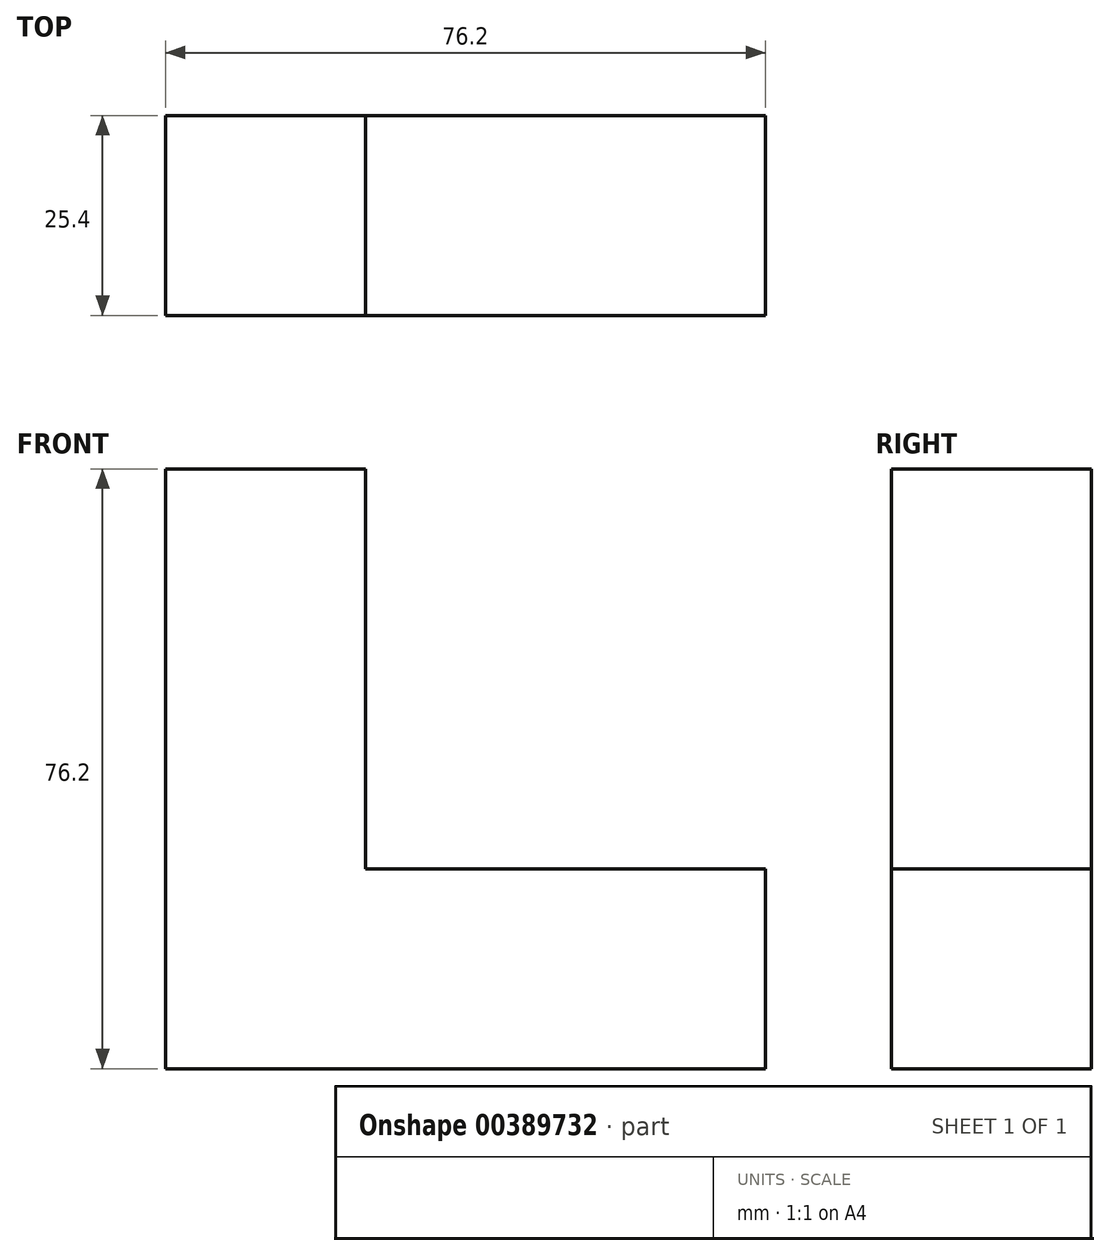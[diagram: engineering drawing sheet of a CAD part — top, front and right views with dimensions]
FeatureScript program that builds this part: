
annotation { "Feature Type Name" : "Feature", "Feature Type Description" : "" }
export const myFeature = defineFeature(function(context is Context, id is Id, definition is map)
    precondition{}
    {
        {
            var Q0;
            Q0=qCreatedBy(makeId("Front.planeOp"),FACE);
            var sketch = newSketch(context, id + "F0", { "sketchPlane" : qUnion([Q0])});
            skLineSegment(sketch, "E0.bottom", {"start": v(0, 0) * mm, "end": v(-25.4, 0) * mm});
            skLineSegment(sketch, "E0.top", {"start": v(0, 25.4) * mm, "end": v(-25.4, 25.4) * mm});
            skLineSegment(sketch, "E0.left", {"start": v(0, 0) * mm, "end": v(0, 25.4) * mm});
            skLineSegment(sketch, "E0.right", {"start": v(-25.4, 0) * mm, "end": v(-25.4, 25.4) * mm});
            skLineSegment(sketch, "E1.top", {"start": v(0, 50.8) * mm, "end": v(-25.4, 50.8) * mm});
            skLineSegment(sketch, "E1.left", {"start": v(0, 25.4) * mm, "end": v(0, 50.8) * mm});
            skLineSegment(sketch, "E1.right", {"start": v(-25.4, 25.4) * mm, "end": v(-25.4, 50.8) * mm});
            skLineSegment(sketch, "E2.top", {"start": v(0, 76.2) * mm, "end": v(-25.4, 76.2) * mm});
            skLineSegment(sketch, "E2.left", {"start": v(0, 50.8) * mm, "end": v(0, 76.2) * mm});
            skLineSegment(sketch, "E2.right", {"start": v(-25.4, 50.8) * mm, "end": v(-25.4, 76.2) * mm});
            skLineSegment(sketch, "E3.bottom", {"start": v(-25.4, 76.2) * mm, "end": v(0, 76.2) * mm});
            skLineSegment(sketch, "E3.top", {"start": v(-25.4, 0) * mm, "end": v(0, 0) * mm});
            skLineSegment(sketch, "E3.left", {"start": v(-25.4, 76.2) * mm, "end": v(-25.4, 0) * mm});
            skLineSegment(sketch, "E3.right", {"start": v(0, 76.2) * mm, "end": v(0, 0) * mm});
            skLineSegment(sketch, "E4.bottom", {"start": v(0, 0) * mm, "end": v(25.4, 0) * mm});
            skLineSegment(sketch, "E4.top", {"start": v(0, 25.4) * mm, "end": v(25.4, 25.4) * mm});
            skLineSegment(sketch, "E4.right", {"start": v(25.4, 0) * mm, "end": v(25.4, 25.4) * mm});
            skLineSegment(sketch, "E5.bottom", {"start": v(25.4, 25.4) * mm, "end": v(50.8, 25.4) * mm});
            skLineSegment(sketch, "E5.top", {"start": v(25.4, 0) * mm, "end": v(50.8, 0) * mm});
            skLineSegment(sketch, "E5.left", {"start": v(25.4, 25.4) * mm, "end": v(25.4, 0) * mm});
            skLineSegment(sketch, "E5.right", {"start": v(50.8, 25.4) * mm, "end": v(50.8, 0) * mm});
            skSolve(sketch);
        }
        {
            var Q0;
            Q0 = qSketchRegion(id + "F0", true);
            extrude(context, id + "F1", {"entities" : qUnion([Q0]), "depth" : 25.4 * mm});
        }
    });
